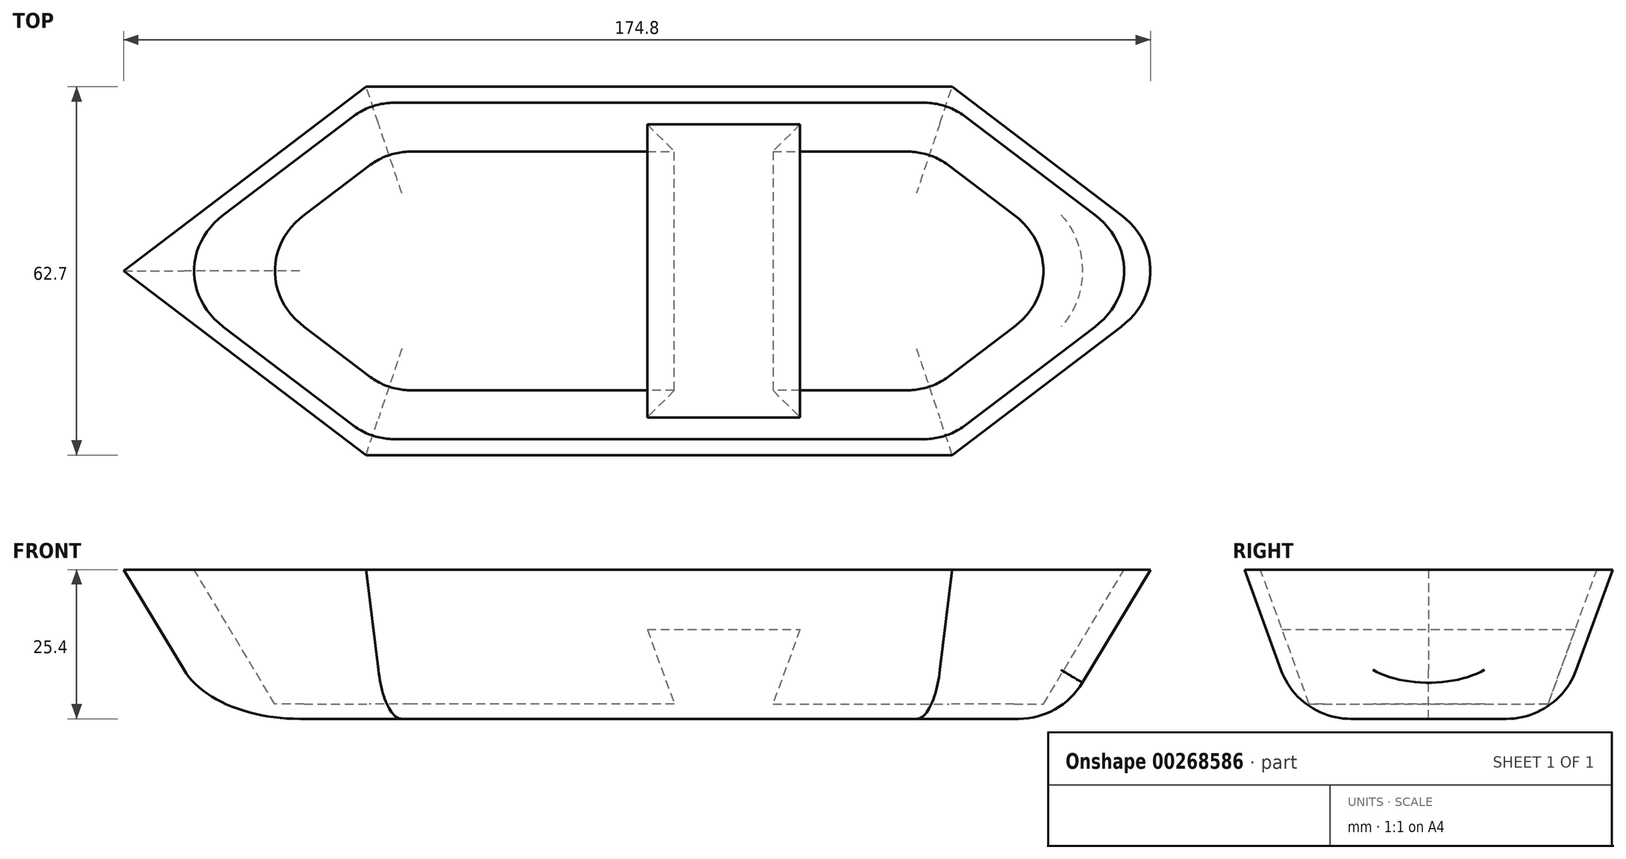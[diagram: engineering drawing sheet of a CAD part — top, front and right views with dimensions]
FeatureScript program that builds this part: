
annotation { "Feature Type Name" : "Feature", "Feature Type Description" : "" }
export const myFeature = defineFeature(function(context is Context, id is Id, definition is map)
    precondition{}
    {
        {
            var Q0;
            Q0=qCreatedBy(makeId("Top.planeOp"),FACE);
            var sketch = newSketch(context, id + "F0", { "sketchPlane" : qUnion([Q0])});
            skLineSegment(sketch, "E0.bottom", {"start": v(-46.78, 22.1) * mm, "end": v(46.78, 22.1) * mm});
            skLineSegment(sketch, "E0.top", {"start": v(-46.78, -22.1) * mm, "end": v(46.78, -22.1) * mm});
            skPoint(sketch, "E0.middle", {"position": v(0, 0) * mm});
            skLineSegment(sketch, "E1", {"start": v(-46.78, 22.1) * mm, "end": v(-75.87, 0) * mm});
            skLineSegment(sketch, "E2", {"start": v(-75.87, 0) * mm, "end": v(-46.78, -22.1) * mm});
            skLineSegment(sketch, "E3", {"start": v(46.78, -22.1) * mm, "end": v(75.87, 0) * mm});
            skLineSegment(sketch, "E4", {"start": v(75.87, 0) * mm, "end": v(46.78, 22.1) * mm});
            skSolve(sketch);
        }
        {
            var Q0;
            Q0=makeQuery(id+"F0.imprint","IMPRINT",FACE,{"disambiguationData":[TD([[makeQuery(id+"F0.imprint","IMPRINT",EDGE,{"derivedFrom":sQuery(id+"F0.wireOp",EDGE,"E0.bottom")}),-1.0]])]});
            extrude(context, id + "F1", {"entities" : qUnion([Q0]), "depth" : 25.4 * mm, "hasDraft" : true, "draftAngle" : 20 * degree});
        }
        {
            var Q0;
            Q0=makeQuery(id+"F1.opExtrude","CAP_FACE",FACE,{"disambiguationData":[OSD([sQuery(id+"F0.wireOp",EDGE,"E0.bottom"),sQuery(id+"F0.wireOp",EDGE,"E0.top"),sQuery(id+"F0.wireOp",EDGE,"E1"),sQuery(id+"F0.wireOp",EDGE,"E2"),sQuery(id+"F0.wireOp",EDGE,"E3"),sQuery(id+"F0.wireOp",EDGE,"E4")])],"isStart":false});
            shell(context, id + "F2", {"entities" : qUnion([Q0]), "thickness" : 2.54 * mm});
        }
        {
            var Q0;
            Q0=makeQuery(id+"F1.opExtrude","CAP_EDGE",EDGE,{"disambiguationData":[OSD([sQuery(id+"F0.wireOp",EDGE,"E0.top")])],"isStart":true});
            var Q1;
            Q1=makeQuery(id+"F1.opExtrude","CAP_EDGE",EDGE,{"disambiguationData":[OSD([sQuery(id+"F0.wireOp",EDGE,"E2")])],"isStart":true});
            var Q2;
            Q2=makeQuery(id+"F1.opExtrude","CAP_EDGE",EDGE,{"disambiguationData":[OSD([sQuery(id+"F0.wireOp",EDGE,"E1")])],"isStart":true});
            var Q3;
            Q3=makeQuery(id+"F1.opExtrude","CAP_EDGE",EDGE,{"disambiguationData":[OSD([sQuery(id+"F0.wireOp",EDGE,"E0.bottom")])],"isStart":true});
            var Q4;
            Q4=makeQuery(id+"F1.opExtrude","CAP_EDGE",EDGE,{"disambiguationData":[OSD([sQuery(id+"F0.wireOp",EDGE,"E4")])],"isStart":true});
            var Q5;
            Q5=makeQuery(id+"F1.opExtrude","CAP_EDGE",EDGE,{"disambiguationData":[OSD([sQuery(id+"F0.wireOp",EDGE,"E3")])],"isStart":true});
            fillet(context, id + "F3", {"entities" : qUnion([Q0, Q1, Q2, Q3, Q4, Q5]), "radius" : 12.7 * mm, "tangentPropagation" : true, "allowEdgeOverflow" : false});
        }
        {
            var Q0;
            Q0=makeQuery(id+"F2.opShell","OFFSET_EDGE",EDGE,{"disambiguationData":[OSD([sQuery(id+"F0.wireOp",EDGE,"E1"),sQuery(id+"F0.wireOp",EDGE,"E2")])]});
            var Q1;
            Q1=makeQuery(id+"F2.opShell","OFFSET_EDGE",EDGE,{"disambiguationData":[OSD([sQuery(id+"F0.wireOp",EDGE,"E3"),sQuery(id+"F0.wireOp",EDGE,"E4")])]});
            var Q2;
            Q2=makeQuery(id+"F2.opShell","OFFSET_EDGE",EDGE,{"disambiguationData":[OSD([sQuery(id+"F0.wireOp",EDGE,"E0.bottom"),sQuery(id+"F0.wireOp",EDGE,"E4")])]});
            var Q3;
            Q3=makeQuery(id+"F2.opShell","OFFSET_EDGE",EDGE,{"disambiguationData":[OSD([sQuery(id+"F0.wireOp",EDGE,"E0.top"),sQuery(id+"F0.wireOp",EDGE,"E3")])]});
            var Q4;
            Q4=makeQuery(id+"F2.opShell","OFFSET_EDGE",EDGE,{"disambiguationData":[OSD([sQuery(id+"F0.wireOp",EDGE,"E0.bottom"),sQuery(id+"F0.wireOp",EDGE,"E1")])]});
            var Q5;
            Q5=makeQuery(id+"F2.opShell","OFFSET_EDGE",EDGE,{"disambiguationData":[OSD([sQuery(id+"F0.wireOp",EDGE,"E0.top"),sQuery(id+"F0.wireOp",EDGE,"E2")])]});
            fillet(context, id + "F4", {"entities" : qUnion([Q0, Q1, Q2, Q3, Q4, Q5]), "radius" : 12.7 * mm, "tangentPropagation" : true, "allowEdgeOverflow" : false});
        }
        {
            var Q0;
            Q0=makeQuery(id+"F2.opShell","OFFSET_FACE",FACE,{"disambiguationData":[OSD([sQuery(id+"F0.wireOp",EDGE,"E0.bottom"),sQuery(id+"F0.wireOp",EDGE,"E0.top"),sQuery(id+"F0.wireOp",EDGE,"E1"),sQuery(id+"F0.wireOp",EDGE,"E2"),sQuery(id+"F0.wireOp",EDGE,"E3"),sQuery(id+"F0.wireOp",EDGE,"E4")])]});
            var sketch = newSketch(context, id + "F5", { "sketchPlane" : qUnion([Q0])});
            skLineSegment(sketch, "E5", {"start": v(2.6, -20.33) * mm, "end": v(2.6, 20.33) * mm});
            skLineSegment(sketch, "E6", {"start": v(2.6, 20.33) * mm, "end": v(19.37, 20.33) * mm});
            skLineSegment(sketch, "E7", {"start": v(19.37, 20.33) * mm, "end": v(19.37, -20.33) * mm});
            skLineSegment(sketch, "E8", {"start": v(19.37, -20.33) * mm, "end": v(2.6, -20.33) * mm});
            skSolve(sketch);
        }
        {
            var Q0;
            Q0=makeQuery(id+"F5.imprint","IMPRINT",FACE,{"disambiguationData":[TD([[makeQuery(id+"F5.imprint","IMPRINT",EDGE,{"derivedFrom":sQuery(id+"F5.wireOp",EDGE,"E5")}),-1.0]])]});
            extrude(context, id + "F6", {"entities" : qUnion([Q0]), "operationType" : NewBodyOperationType.ADD, "depth" : 12.7 * mm, "hasDraft" : true, "draftAngle" : 20 * degree});
        }
        {
            var Q0;
            Q0=makeQuery(id+"F1.opExtrude","SWEPT_EDGE",EDGE,{"disambiguationData":[OSD([sQuery(id+"F0.wireOp",EDGE,"E3"),sQuery(id+"F0.wireOp",EDGE,"E4")])]});
            fillet(context, id + "F7", {"entities" : qUnion([Q0]), "radius" : 12.7 * mm, "tangentPropagation" : true, "allowEdgeOverflow" : false});
        }
    });
